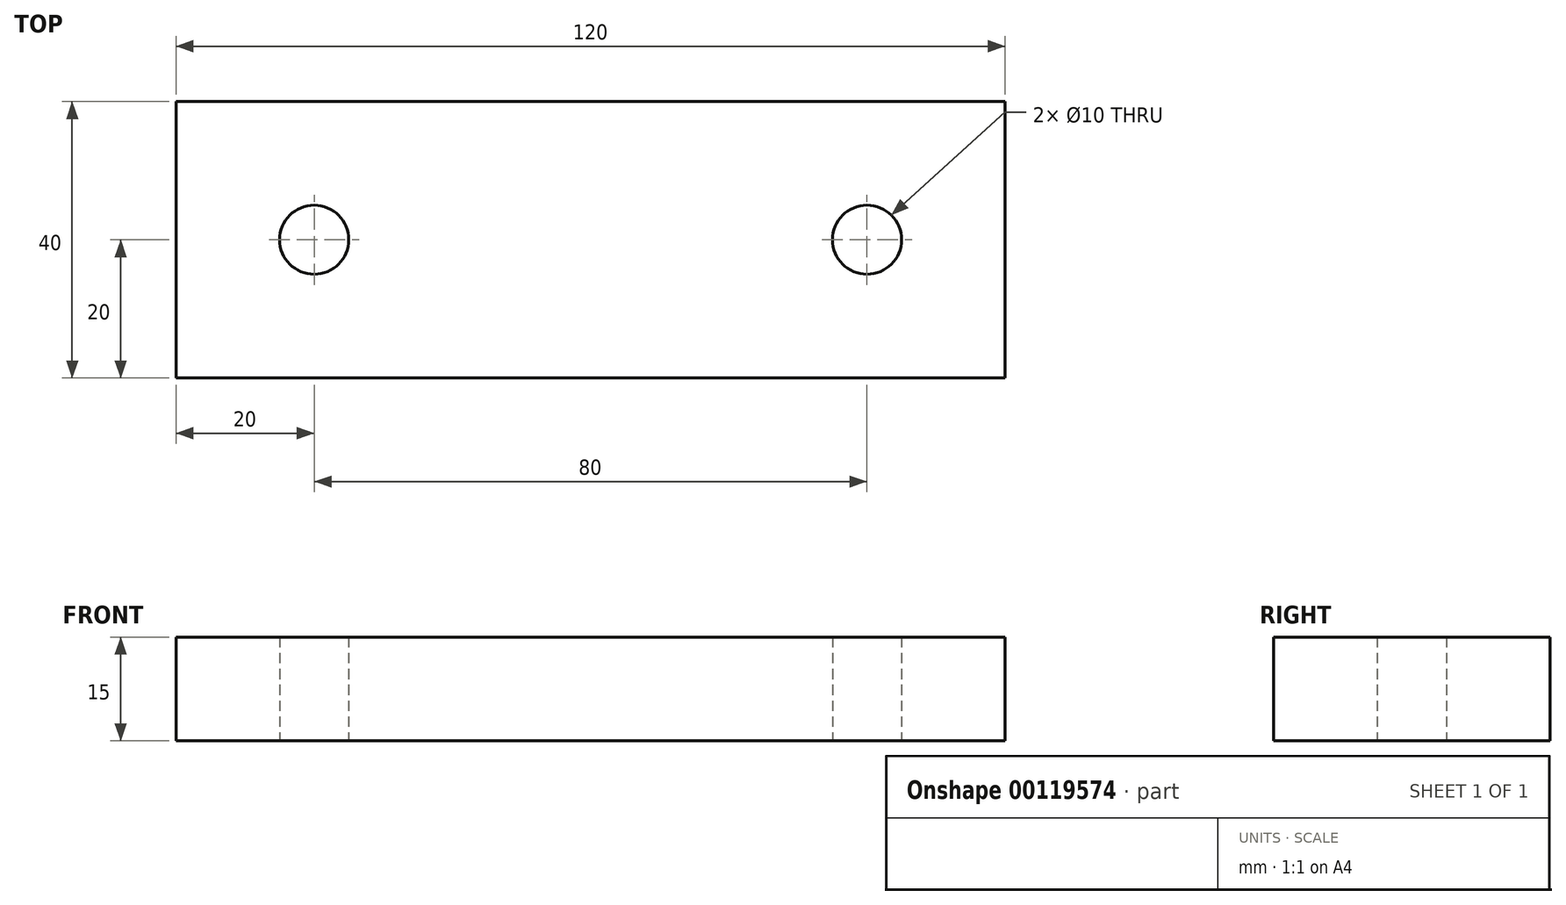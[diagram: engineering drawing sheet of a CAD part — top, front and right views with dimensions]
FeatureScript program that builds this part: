
annotation { "Feature Type Name" : "Feature", "Feature Type Description" : "" }
export const myFeature = defineFeature(function(context is Context, id is Id, definition is map)
    precondition{}
    {
        {
            var Q0;
            Q0=qCreatedBy(makeId("Top.planeOp"),FACE);
            var sketch = newSketch(context, id + "F0", { "sketchPlane" : qUnion([Q0])});
            skLineSegment(sketch, "E0.bottom", {"start": v(0, 0) * mm, "end": v(-120, 0) * mm});
            skLineSegment(sketch, "E0.top", {"start": v(0, 40) * mm, "end": v(-120, 40) * mm});
            skLineSegment(sketch, "E0.left", {"start": v(0, 0) * mm, "end": v(0, 40) * mm});
            skLineSegment(sketch, "E0.right", {"start": v(-120, 0) * mm, "end": v(-120, 40) * mm});
            skLineSegment(sketch, "E1", {"start": v(0, 40) * mm, "end": v(0, 20) * mm, "construction": true});
            skLineSegment(sketch, "E2", {"start": v(0, 20) * mm, "end": v(-20, 20) * mm, "construction": true});
            skCircle(sketch, "E3", {"center": v(-20, 20) * mm, "radius": 5 * mm});
            skLineSegment(sketch, "E4", {"start": v(-20, 20) * mm, "end": v(-100, 20) * mm, "construction": true});
            skCircle(sketch, "E5", {"center": v(-100, 20) * mm, "radius": 5 * mm});
            skSolve(sketch);
        }
        {
            var Q0;
            Q0 = qSketchRegion(id + "F0", true);
            extrude(context, id + "F1", {"entities" : qUnion([Q0]), "depth" : 15 * mm});
        }
    });
